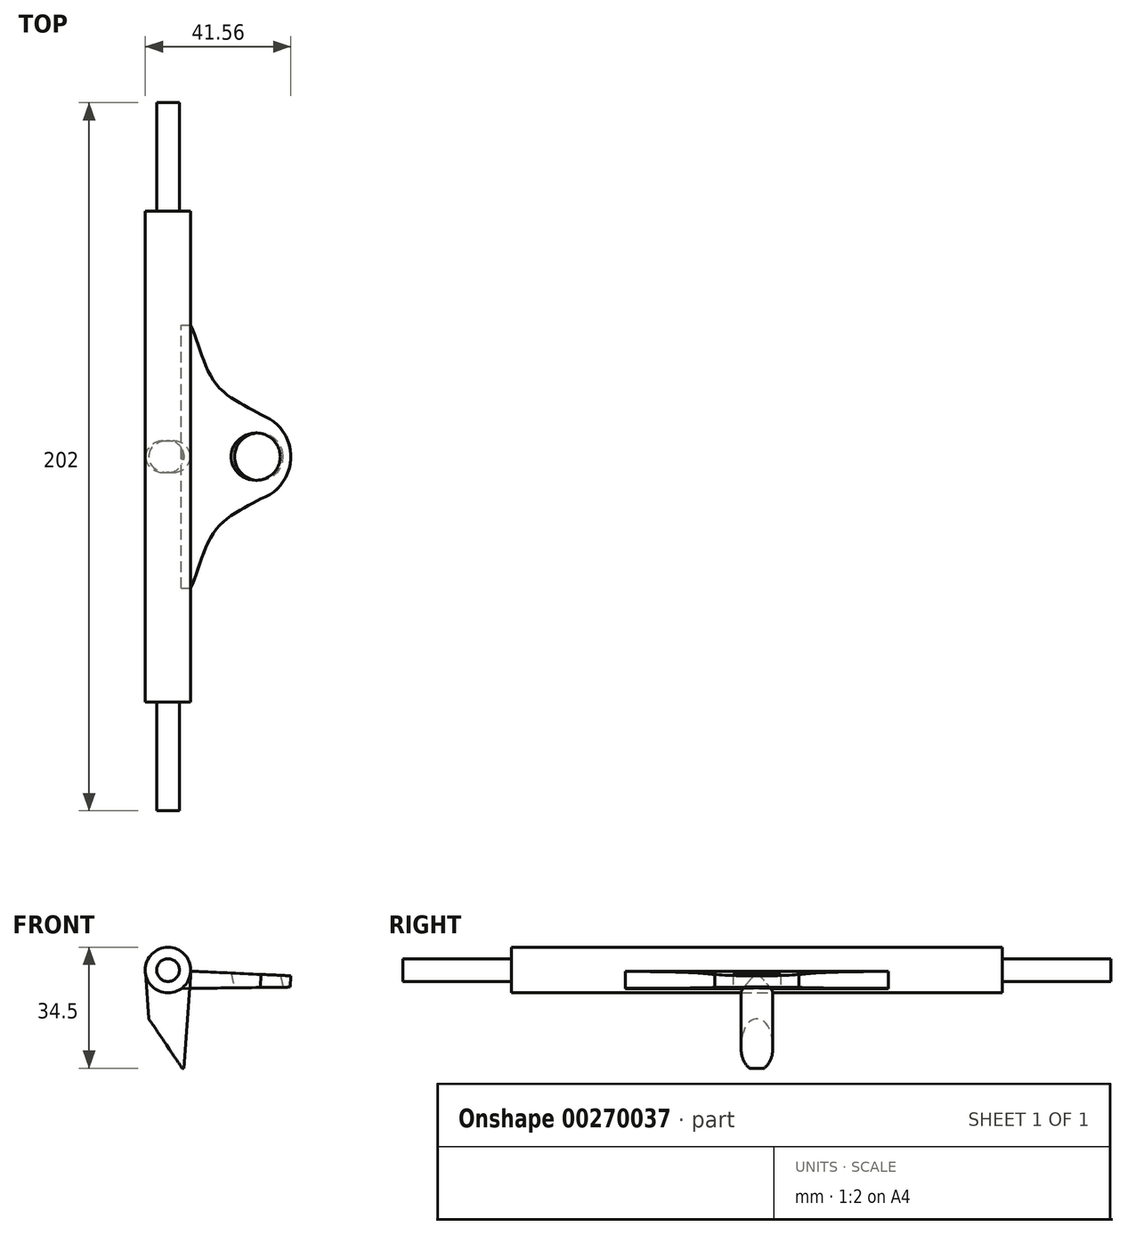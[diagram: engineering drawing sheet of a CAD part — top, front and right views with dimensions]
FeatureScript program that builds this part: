
annotation { "Feature Type Name" : "Feature", "Feature Type Description" : "" }
export const myFeature = defineFeature(function(context is Context, id is Id, definition is map)
    precondition{}
    {
        {
            var Q0;
            Q0=qCreatedBy(makeId("Front.planeOp"),FACE);
            var sketch = newSketch(context, id + "F0", { "sketchPlane" : qUnion([Q0])});
            skCircle(sketch, "E0", {"center": v(0, 0) * mm, "radius": 6.5 * mm});
            skSolve(sketch);
        }
        {
            var Q0;
            Q0 = qSketchRegion(id + "F0", true);
            extrude(context, id + "F1", {"entities" : qUnion([Q0]), "endBound" : BoundingType.SYMMETRIC, "depth" : 140 * mm});
        }
        {
            var Q0;
            Q0=qCreatedBy(makeId("Front.planeOp"),FACE);
            var sketch = newSketch(context, id + "F2", { "sketchPlane" : qUnion([Q0])});
            skCircle(sketch, "E1.0.0", {"center": v(0, 0) * mm, "radius": 6.5 * mm});
            skLineSegment(sketch, "E2", {"start": v(-6.5, 0) * mm, "end": v(6.5, 0) * mm});
            skLineSegment(sketch, "E3", {"start": v(0, 0) * mm, "end": v(0, -28) * mm, "construction": true});
            skLineSegment(sketch, "E4", {"start": v(0, -28) * mm, "end": v(-4.5, -28) * mm});
            skLineSegment(sketch, "E5.MirrorCS", {"start": v(0, -28) * mm, "end": v(4.5, -28) * mm});
            skLineSegment(sketch, "E6", {"start": v(-6.5, 0) * mm, "end": v(-4.5, -28) * mm});
            skLineSegment(sketch, "E7", {"start": v(4.5, -28) * mm, "end": v(6.5, 0) * mm});
            skSolve(sketch);
        }
        {
            var Q0;
            {var subQ1=sQuery(id+"F2.wireOp",EDGE,"E4");Q0=makeQuery(id+"F2.imprint","IMPRINT",FACE,{"disambiguationData":[TD([[makeQuery(id+"F2.imprint","IMPRINT",EDGE,{"derivedFrom":subQ1}),-1.0]])]});}
            extrude(context, id + "F3", {"entities" : qUnion([Q0]), "endBound" : BoundingType.SYMMETRIC, "depth" : 9 * mm});
        }
        {
            var Q0;
            Q0=makeQuery(id+"F3.opExtrude","CAP_EDGE",EDGE,{"disambiguationData":[OSD([sQuery(id+"F2.wireOp",EDGE,"E7")])],"isStart":false});
            var Q1;
            Q1=makeQuery(id+"F3.opExtrude","CAP_EDGE",EDGE,{"disambiguationData":[OSD([sQuery(id+"F2.wireOp",EDGE,"E7")])],"isStart":true});
            var Q2;
            Q2=makeQuery(id+"F3.opExtrude","CAP_EDGE",EDGE,{"disambiguationData":[OSD([sQuery(id+"F2.wireOp",EDGE,"E6")])],"isStart":false});
            var Q3;
            Q3=makeQuery(id+"F3.opExtrude","CAP_EDGE",EDGE,{"disambiguationData":[OSD([sQuery(id+"F2.wireOp",EDGE,"E6")])],"isStart":true});
            fillet(context, id + "F4", {"entities" : qUnion([Q0, Q1, Q2, Q3]), "radius" : 4.5 * mm, "tangentPropagation" : true, "allowEdgeOverflow" : false});
        }
        {
            var Q0;
            Q0=makeQuery(id+"F0.imprint","IMPRINT",FACE,{"disambiguationData":[TD([[makeQuery(id+"F0.imprint","IMPRINT",EDGE,{"derivedFrom":sQuery(id+"F0.wireOp",EDGE,"E0")}),1.0]])]});
            var sketch = newSketch(context, id + "F5", { "sketchPlane" : qUnion([Q0])});
            skLineSegment(sketch, "E8", {"start": v(0, 0) * mm, "end": v(0, -6.5) * mm});
            skLineSegment(sketch, "E9", {"start": v(0, 0) * mm, "end": v(35.06, -1.64) * mm});
            skLineSegment(sketch, "E10.MirrorCS", {"start": v(0, -5.32) * mm, "end": v(35.06, -4.86) * mm});
            skLineSegment(sketch, "E11", {"start": v(35.06, -4.86) * mm, "end": v(35.06, -1.64) * mm});
            skSolve(sketch);
        }
        {
            var Q0;
            {var subQ0=sQuery(id+"F5.wireOp",EDGE,"E11");Q0=makeQuery(id+"F5.imprint","IMPRINT",FACE,{"disambiguationData":[TD([[makeQuery(id+"F5.imprint","IMPRINT",EDGE,{"derivedFrom":subQ0}),1.0]])]});}
            extrude(context, id + "F6", {"entities" : qUnion([Q0]), "endBound" : BoundingType.SYMMETRIC, "depth" : 75 * mm});
        }
        {
            var Q0;
            Q0=makeQuery(id+"F6.opExtrude","SWEPT_FACE",FACE,{"disambiguationData":[OSD([sQuery(id+"F5.wireOp",EDGE,"E9")])]});
            var sketch = newSketch(context, id + "F7", { "sketchPlane" : qUnion([Q0])});
            skLineSegment(sketch, "E12", {"start": v(0, 0) * mm, "end": v(35.1, 0) * mm, "construction": true});
            skLineSegment(sketch, "E13", {"start": v(36.25, -37.5) * mm, "end": v(36.25, 37.5) * mm});
            skLineSegment(sketch, "E14", {"start": v(0, 46.37) * mm, "end": v(0, -46.37) * mm});
            skLineSegment(sketch, "E15", {"start": v(0, 46.37) * mm, "end": v(36.25, 46.37) * mm});
            skLineSegment(sketch, "E16", {"start": v(36.25, 46.37) * mm, "end": v(36.25, 37.5) * mm});
            skLineSegment(sketch, "E17", {"start": v(0, -46.37) * mm, "end": v(36.25, -46.37) * mm});
            skLineSegment(sketch, "E18", {"start": v(36.25, -46.37) * mm, "end": v(36.25, -37.5) * mm});
            skFitSpline(sketch, "E19", {"points": [v(0, 46.37) * mm, v(6.5, 37.5) * mm, v(13.76, 20.7) * mm, v(26.6, 11.95) * mm], "startDerivative": vector(23.86, -26) * mm, "endDerivative": vector(36.6, -22.3) * mm});
            skFitSpline(sketch, "E20.MirrorCS", {"points": [v(0, -46.37) * mm, v(6.5, -37.5) * mm, v(13.76, -20.7) * mm, v(26.6, -11.95) * mm], "startDerivative": vector(23.86, 26) * mm, "endDerivative": vector(36.6, 22.3) * mm});
            skArc(sketch, "E21", {"start": v(26.6, -11.95) * mm, "mid": v(35.1, 0) * mm, "end": v(26.6, 11.95) * mm});
            skSolve(sketch);
        }
        {
            var Q0;
            {var subQ1=sQuery(id+"F5.wireOp",EDGE,"E9");var subQ2=makeQuery(id+"F6.opExtrude","CAP_EDGE",EDGE,{"disambiguationData":[OSD([subQ1])],"isStart":true});Q0=makeQuery(id+"F7.imprint","IMPRINT",FACE,{"disambiguationData":[TD([[makeQuery(id+"F7.imprint","IMPRINT",EDGE,{"derivedFrom":subQ2}),-1.0]])]});}
            var Q1;
            {var subQ1=sQuery(id+"F5.wireOp",EDGE,"E9");var subQ2=makeQuery(id+"F6.opExtrude","CAP_EDGE",EDGE,{"disambiguationData":[OSD([subQ1])],"isStart":false});Q1=makeQuery(id+"F7.imprint","IMPRINT",FACE,{"disambiguationData":[TD([[makeQuery(id+"F7.imprint","IMPRINT",EDGE,{"derivedFrom":subQ2}),1.0]])]});}
            var Q2;
            Q2=makeQuery(id+"F6.opExtrude","SWEPT_FACE",FACE,{"disambiguationData":[OSD([sQuery(id+"F5.wireOp",EDGE,"E11")])]});
            extrude(context, id + "F8", {"entities" : qUnion([Q0, Q1, Q2]), "operationType" : NewBodyOperationType.REMOVE, "oppositeDirection" : true, "depth" : 25 * mm});
        }
        {
            var Q0;
            Q0=makeQuery(id+"F1.opExtrude","CAP_FACE",FACE,{"disambiguationData":[OSD([sQuery(id+"F0.wireOp",EDGE,"E0")])],"isStart":false});
            var sketch = newSketch(context, id + "F9", { "sketchPlane" : qUnion([Q0])});
            skCircle(sketch, "E22.0.0", {"center": v(0, 0) * mm, "radius": 6.5 * mm});
            skCircle(sketch, "E23", {"center": v(0, 0) * mm, "radius": 3.25 * mm});
            skSolve(sketch);
        }
        {
            var Q0;
            Q0=makeQuery(id+"F9.imprint","IMPRINT",FACE,{"disambiguationData":[TD([[makeQuery(id+"F9.imprint","IMPRINT",EDGE,{"derivedFrom":sQuery(id+"F9.wireOp",EDGE,"E23")}),1.0]])]});
            extrude(context, id + "F10", {"entities" : qUnion([Q0]), "operationType" : NewBodyOperationType.ADD, "depth" : 31 * mm});
        }
        {
            var Q0;
            Q0=makeQuery(id+"F1.opExtrude","CAP_FACE",FACE,{"disambiguationData":[OSD([sQuery(id+"F0.wireOp",EDGE,"E0")])],"isStart":true});
            var sketch = newSketch(context, id + "F11", { "sketchPlane" : qUnion([Q0])});
            skCircle(sketch, "E24.0.0", {"center": v(0, 0) * mm, "radius": 6.5 * mm});
            skCircle(sketch, "E25", {"center": v(0, 0) * mm, "radius": 3.25 * mm});
            skSolve(sketch);
        }
        {
            var Q0;
            Q0=makeQuery(id+"F11.imprint","IMPRINT",FACE,{"disambiguationData":[TD([[makeQuery(id+"F11.imprint","IMPRINT",EDGE,{"derivedFrom":sQuery(id+"F11.wireOp",EDGE,"E25")}),1.0]])]});
            extrude(context, id + "F12", {"entities" : qUnion([Q0]), "operationType" : NewBodyOperationType.ADD, "depth" : 31 * mm});
        }
        {
            var Q0;
            Q0=qCreatedBy(makeId("Front.planeOp"),FACE);
            var sketch = newSketch(context, id + "F13", { "sketchPlane" : qUnion([Q0])});
            skLineSegment(sketch, "E26", {"start": v(-28.2, -30.78) * mm, "end": v(5.9, -30.78) * mm});
            skLineSegment(sketch, "E27", {"start": v(5.9, -30.78) * mm, "end": v(-14.7, -0.25) * mm});
            skLineSegment(sketch, "E28", {"start": v(-14.7, -0.25) * mm, "end": v(-28.2, -30.78) * mm});
            skSolve(sketch);
        }
        {
            var Q0;
            Q0 = qSketchRegion(id + "F13", true);
            var Q1;
            Q1=makeQuery(id+"F13.imprint","IMPRINT",FACE,{"disambiguationData":[TD([[makeQuery(id+"F13.imprint","IMPRINT",EDGE,{"derivedFrom":sQuery(id+"F13.wireOp",EDGE,"E26")}),1.0]])]});
            extrude(context, id + "F14", {"entities" : qUnion([Q0, Q1]), "operationType" : NewBodyOperationType.REMOVE, "endBound" : BoundingType.SYMMETRIC, "oppositeDirection" : true, "depth" : 25 * mm});
        }
        {
            var Q0;
            Q0=makeQuery(id+"F6.opExtrude","SWEPT_FACE",FACE,{"disambiguationData":[OSD([sQuery(id+"F5.wireOp",EDGE,"E9")])]});
            var sketch = newSketch(context, id + "F15", { "sketchPlane" : qUnion([Q0])});
            skLineSegment(sketch, "E29.0.0", {"start": v(6.5, 37.5) * mm, "end": v(6.5, -37.5) * mm});
            skFitSpline(sketch, "E29.0.1", {"points": [v(0, -46.37) * mm, v(2.29, -43.88) * mm, v(7.81, -38.12) * mm, v(11.32, -18.61) * mm, v(22.43, -14.5) * mm, v(26.6, -11.95) * mm]});
            skArc(sketch, "E29.0.2", {"start": v(26.6, -11.95) * mm, "mid": v(35.1, 0) * mm, "end": v(26.6, 11.95) * mm});
            skFitSpline(sketch, "E29.0.3", {"points": [v(26.6, 11.95) * mm, v(22.43, 14.5) * mm, v(11.32, 18.61) * mm, v(7.81, 38.12) * mm, v(2.29, 43.88) * mm, v(0, 46.37) * mm]});
            skCircle(sketch, "E30", {"center": v(25.1, -0.1) * mm, "radius": 7 * mm});
            skSolve(sketch);
        }
        {
            var Q0;
            Q0=qCreatedBy(makeId("Front.planeOp"),FACE);
            var sketch = newSketch(context, id + "F16", { "sketchPlane" : qUnion([Q0])});
            skLineSegment(sketch, "E31", {"start": v(18.08, -0.85) * mm, "end": v(23, -22.7) * mm});
            skLineSegment(sketch, "E32", {"start": v(23, -22.7) * mm, "end": v(37.24, -23.37) * mm});
            skLineSegment(sketch, "E33", {"start": v(37.24, -23.37) * mm, "end": v(32.06, -1.5) * mm});
            skLineSegment(sketch, "E34", {"start": v(18.08, -0.85) * mm, "end": v(14.88, 12.65) * mm});
            skLineSegment(sketch, "E35", {"start": v(14.88, 12.65) * mm, "end": v(28.87, 12) * mm});
            skLineSegment(sketch, "E36", {"start": v(28.87, 12) * mm, "end": v(32.06, -1.5) * mm});
            skLineSegment(sketch, "E37", {"start": v(30.12, -23.03) * mm, "end": v(21.87, 12.32) * mm});
            skSolve(sketch);
        }
        {
            var Q0;
            {var subQ3=sQuery(id+"F16.wireOp",EDGE,"E33");Q0=makeQuery(id+"F16.imprint","IMPRINT",FACE,{"disambiguationData":[TD([[makeQuery(id+"F16.imprint","IMPRINT",EDGE,{"derivedFrom":subQ3}),1.0]])]});}
            var Q1;
            Q1=sQuery(id+"F16.wireOp",EDGE,"E37");
            revolve(context, id + "F17", {"operationType" : NewBodyOperationType.REMOVE, "entities" : qUnion([Q0]), "axis" : qUnion([Q1]), "revolveType" : RevolveType.FULL, "oppositeDirection" : true});
        }
    });
